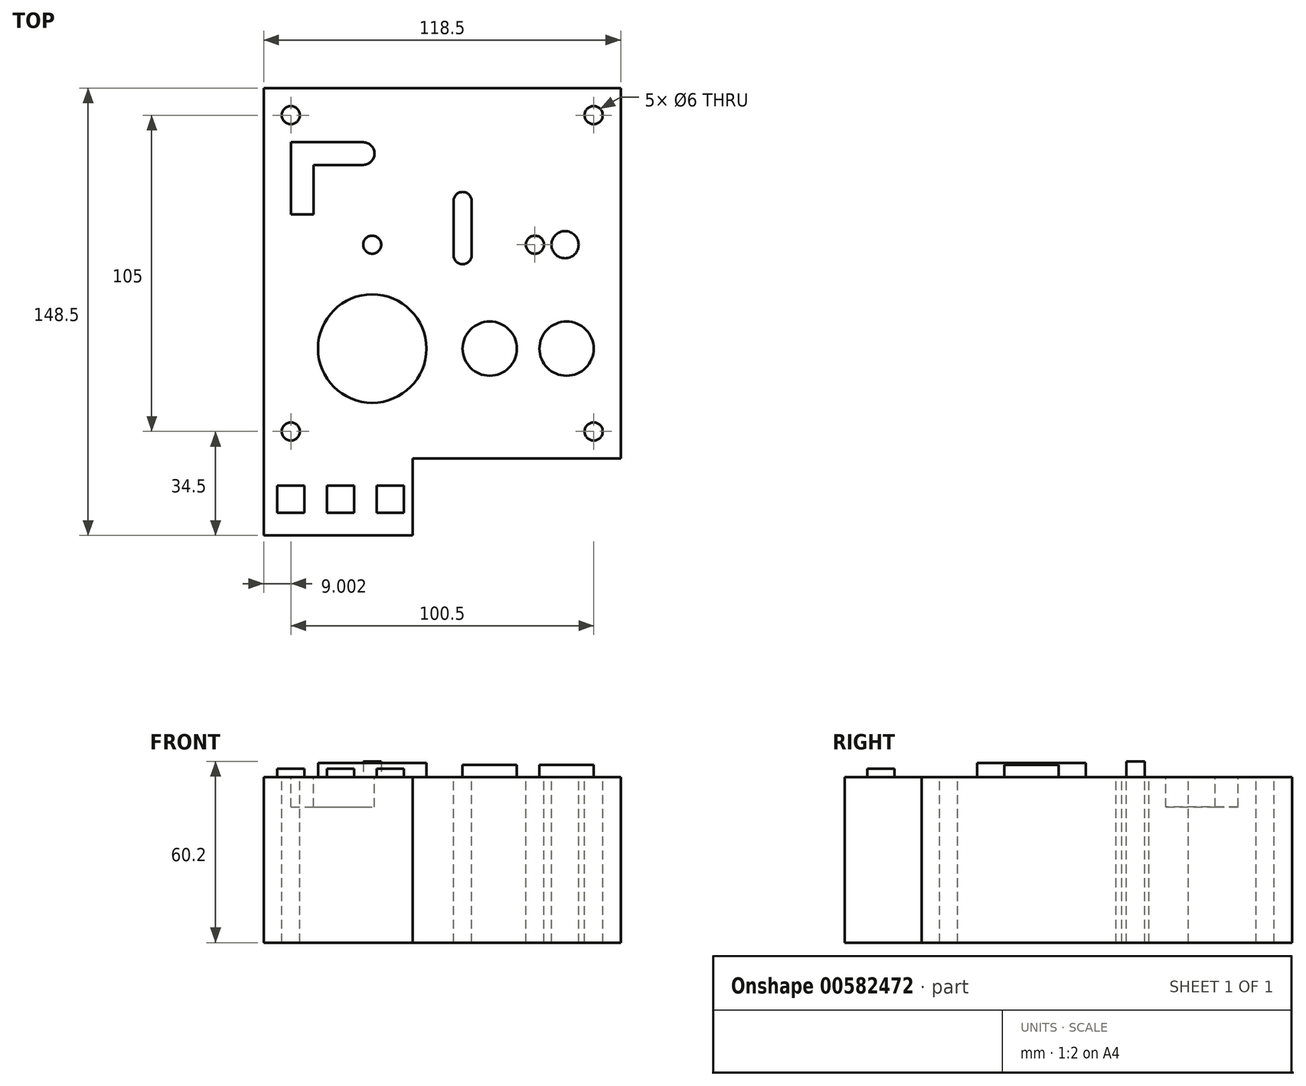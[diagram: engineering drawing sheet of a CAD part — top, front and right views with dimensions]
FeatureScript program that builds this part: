
annotation { "Feature Type Name" : "Feature", "Feature Type Description" : "" }
export const myFeature = defineFeature(function(context is Context, id is Id, definition is map)
    precondition{}
    {
        {
            var Q0;
            Q0=qCreatedBy(makeId("Top.planeOp"),FACE);
            var sketch = newSketch(context, id + "F0", { "sketchPlane" : qUnion([Q0])});
            skLineSegment(sketch, "E0", {"start": v(-56.89, 15.26) * mm, "end": v(61.61, 15.26) * mm});
            skLineSegment(sketch, "E1", {"start": v(61.61, 15.26) * mm, "end": v(61.61, -107.74) * mm});
            skLineSegment(sketch, "E2", {"start": v(-56.89, 15.26) * mm, "end": v(-56.89, -133.24) * mm});
            skLineSegment(sketch, "E3", {"start": v(-56.89, -133.24) * mm, "end": v(-7.39, -133.24) * mm});
            skLineSegment(sketch, "E4", {"start": v(61.61, -107.74) * mm, "end": v(-7.39, -107.74) * mm});
            skLineSegment(sketch, "E5", {"start": v(-7.39, -107.74) * mm, "end": v(-7.39, -133.24) * mm});
            skSolve(sketch);
        }
        {
            var Q0;
            Q0=makeQuery(id+"F0.imprint","IMPRINT",FACE,{"disambiguationData":[TD([[makeQuery(id+"F0.imprint","IMPRINT",EDGE,{"derivedFrom":sQuery(id+"F0.wireOp",EDGE,"E0")}),-1.0]])]});
            extrude(context, id + "F1", {"entities" : qUnion([Q0]), "depth" : 55 * mm, "offsetDistance" : 25 * mm});
        }
        {
            var Q0;
            Q0=makeQuery(id+"F1.opExtrude","CAP_FACE",FACE,{"disambiguationData":[OSD([sQuery(id+"F0.wireOp",EDGE,"E0"),sQuery(id+"F0.wireOp",EDGE,"E1"),sQuery(id+"F0.wireOp",EDGE,"E2"),sQuery(id+"F0.wireOp",EDGE,"E3"),sQuery(id+"F0.wireOp",EDGE,"E4"),sQuery(id+"F0.wireOp",EDGE,"E5")])],"isStart":false});
            var sketch = newSketch(context, id + "F2", { "sketchPlane" : qUnion([Q0])});
            skCircle(sketch, "E6", {"center": v(52.61, 6.26) * mm, "radius": 3 * mm});
            skLineSegment(sketch, "E7", {"start": v(52.61, 6.26) * mm, "end": v(49.61, 6.26) * mm});
            skCircle(sketch, "E8", {"center": v(-47.89, -98.74) * mm, "radius": 3 * mm});
            skCircle(sketch, "E9", {"center": v(-47.89, 6.26) * mm, "radius": 3 * mm});
            skCircle(sketch, "E10", {"center": v(52.61, -98.74) * mm, "radius": 3 * mm});
            skPoint(sketch, "E11.end.orphan", {"position": v(52.61, 15.26) * mm});
            skSolve(sketch);
        }
        {
            var Q0;
            Q0=makeQuery(id+"F2.imprint","IMPRINT",FACE,{"disambiguationData":[TD([[makeQuery(id+"F2.imprint","IMPRINT",EDGE,{"derivedFrom":sQuery(id+"F2.wireOp",EDGE,"E8")}),1.0]])]});
            var Q1;
            Q1=makeQuery(id+"F2.imprint","IMPRINT",FACE,{"disambiguationData":[TD([[makeQuery(id+"F2.imprint","IMPRINT",EDGE,{"derivedFrom":sQuery(id+"F2.wireOp",EDGE,"E10")}),1.0]])]});
            var Q2;
            Q2=makeQuery(id+"F2.imprint","IMPRINT",FACE,{"disambiguationData":[TD([[makeQuery(id+"F2.imprint","IMPRINT",EDGE,{"derivedFrom":sQuery(id+"F2.wireOp",EDGE,"E6")}),1.0]])]});
            var Q3;
            Q3=makeQuery(id+"F2.imprint","IMPRINT",FACE,{"disambiguationData":[TD([[makeQuery(id+"F2.imprint","IMPRINT",EDGE,{"derivedFrom":sQuery(id+"F2.wireOp",EDGE,"E9")}),1.0]])]});
            extrude(context, id + "F3", {"entities" : qUnion([Q0, Q1, Q2, Q3]), "operationType" : NewBodyOperationType.REMOVE, "endBound" : BoundingType.THROUGH_ALL, "oppositeDirection" : true, "depth" : 55 * mm, "offsetDistance" : 25 * mm});
        }
        {
            var Q0;
            Q0=makeQuery(id+"F1.opExtrude","CAP_FACE",FACE,{"disambiguationData":[OSD([sQuery(id+"F0.wireOp",EDGE,"E0"),sQuery(id+"F0.wireOp",EDGE,"E1"),sQuery(id+"F0.wireOp",EDGE,"E2"),sQuery(id+"F0.wireOp",EDGE,"E3"),sQuery(id+"F0.wireOp",EDGE,"E4"),sQuery(id+"F0.wireOp",EDGE,"E5")])],"isStart":false});
            var sketch = newSketch(context, id + "F4", { "sketchPlane" : qUnion([Q0])});
            skLineSegment(sketch, "E12", {"start": v(61.61, 15.26) * mm, "end": v(61.61, -71.24) * mm});
            skCircle(sketch, "E13", {"center": v(-20.89, -71.24) * mm, "radius": 18 * mm});
            skPoint(sketch, "E14.orphan", {"position": v(-56.89, -71.24) * mm});
            skSolve(sketch);
        }
        {
            var Q0;
            Q0 = qSketchRegion(id + "F4", true);
            extrude(context, id + "F5", {"entities" : qUnion([Q0]), "operationType" : NewBodyOperationType.ADD, "depth" : 4.7 * mm, "offsetDistance" : 25 * mm});
        }
        {
            var Q0;
            Q0=makeQuery(id+"F1.opExtrude","CAP_FACE",FACE,{"disambiguationData":[OSD([sQuery(id+"F0.wireOp",EDGE,"E0"),sQuery(id+"F0.wireOp",EDGE,"E1"),sQuery(id+"F0.wireOp",EDGE,"E2"),sQuery(id+"F0.wireOp",EDGE,"E3"),sQuery(id+"F0.wireOp",EDGE,"E4"),sQuery(id+"F0.wireOp",EDGE,"E5")])],"isStart":false});
            var sketch = newSketch(context, id + "F6", { "sketchPlane" : qUnion([Q0])});
            skCircle(sketch, "E15", {"center": v(18.11, -71.24) * mm, "radius": 9 * mm});
            skCircle(sketch, "E16", {"center": v(43.61, -71.24) * mm, "radius": 9 * mm});
            skPoint(sketch, "E17.orphan", {"position": v(-20.89, -71.24) * mm});
            skSolve(sketch);
        }
        {
            var Q0;
            Q0=makeQuery(id+"F6.imprint","IMPRINT",FACE,{"disambiguationData":[TD([[makeQuery(id+"F6.imprint","IMPRINT",EDGE,{"derivedFrom":sQuery(id+"F6.wireOp",EDGE,"E15")}),1.0]])]});
            var Q1;
            Q1=makeQuery(id+"F6.imprint","IMPRINT",FACE,{"disambiguationData":[TD([[makeQuery(id+"F6.imprint","IMPRINT",EDGE,{"derivedFrom":sQuery(id+"F6.wireOp",EDGE,"E16")}),1.0]])]});
            extrude(context, id + "F7", {"entities" : qUnion([Q0, Q1]), "operationType" : NewBodyOperationType.ADD, "depth" : 4 * mm, "offsetDistance" : 25 * mm});
        }
        {
            var Q0;
            Q0=makeQuery(id+"F1.opExtrude","CAP_FACE",FACE,{"disambiguationData":[OSD([sQuery(id+"F0.wireOp",EDGE,"E0"),sQuery(id+"F0.wireOp",EDGE,"E1"),sQuery(id+"F0.wireOp",EDGE,"E2"),sQuery(id+"F0.wireOp",EDGE,"E3"),sQuery(id+"F0.wireOp",EDGE,"E4"),sQuery(id+"F0.wireOp",EDGE,"E5")])],"isStart":false});
            var sketch = newSketch(context, id + "F8", { "sketchPlane" : qUnion([Q0])});
            skLineSegment(sketch, "E18", {"start": v(-56.89, 15.26) * mm, "end": v(9.11, 15.26) * mm});
            skArc(sketch, "E19", {"start": v(12.11, -22.24) * mm, "mid": v(9.11, -19.24) * mm, "end": v(6.11, -22.24) * mm});
            skArc(sketch, "E20", {"start": v(6.11, -40.24) * mm, "mid": v(9.11, -43.24) * mm, "end": v(12.11, -40.24) * mm});
            skLineSegment(sketch, "E21", {"start": v(6.11, -22.24) * mm, "end": v(6.11, -40.24) * mm});
            skLineSegment(sketch, "E22", {"start": v(12.11, -22.24) * mm, "end": v(12.11, -40.24) * mm});
            skSolve(sketch);
        }
        {
            var Q0;
            Q0=makeQuery(id+"F8.imprint","IMPRINT",FACE,{"disambiguationData":[TD([[makeQuery(id+"F8.imprint","IMPRINT",EDGE,{"derivedFrom":sQuery(id+"F8.wireOp",EDGE,"E19")}),1.0]])]});
            extrude(context, id + "F9", {"entities" : qUnion([Q0]), "operationType" : NewBodyOperationType.REMOVE, "endBound" : BoundingType.THROUGH_ALL, "oppositeDirection" : true, "depth" : 25 * mm, "offsetDistance" : 25 * mm});
        }
        {
            var Q0;
            Q0=makeQuery(id+"F1.opExtrude","CAP_FACE",FACE,{"disambiguationData":[OSD([sQuery(id+"F0.wireOp",EDGE,"E0"),sQuery(id+"F0.wireOp",EDGE,"E1"),sQuery(id+"F0.wireOp",EDGE,"E2"),sQuery(id+"F0.wireOp",EDGE,"E3"),sQuery(id+"F0.wireOp",EDGE,"E4"),sQuery(id+"F0.wireOp",EDGE,"E5")])],"isStart":false});
            var sketch = newSketch(context, id + "F10", { "sketchPlane" : qUnion([Q0])});
            skLineSegment(sketch, "E23", {"start": v(-56.89, 15.26) * mm, "end": v(33.11, 15.26) * mm});
            skCircle(sketch, "E24", {"center": v(33.11, -36.74) * mm, "radius": 3 * mm});
            skCircle(sketch, "E25", {"center": v(43.11, -36.74) * mm, "radius": 4.5 * mm});
            skSolve(sketch);
        }
        {
            var Q0;
            Q0 = qSketchRegion(id + "F10", true);
            extrude(context, id + "F11", {"entities" : qUnion([Q0]), "operationType" : NewBodyOperationType.REMOVE, "endBound" : BoundingType.THROUGH_ALL, "oppositeDirection" : true, "depth" : 25 * mm, "offsetDistance" : 25 * mm});
        }
        {
            var Q0;
            Q0=makeQuery(id+"F1.opExtrude","CAP_FACE",FACE,{"disambiguationData":[OSD([sQuery(id+"F0.wireOp",EDGE,"E0"),sQuery(id+"F0.wireOp",EDGE,"E1"),sQuery(id+"F0.wireOp",EDGE,"E2"),sQuery(id+"F0.wireOp",EDGE,"E3"),sQuery(id+"F0.wireOp",EDGE,"E4"),sQuery(id+"F0.wireOp",EDGE,"E5")])],"isStart":false});
            var sketch = newSketch(context, id + "F12", { "sketchPlane" : qUnion([Q0])});
            skLineSegment(sketch, "E26", {"start": v(-47.89, -2.74) * mm, "end": v(-23.89, -2.74) * mm});
            skArc(sketch, "E27", {"start": v(-23.89, -10.24) * mm, "mid": v(-20.14, -6.5) * mm, "end": v(-23.89, -2.74) * mm});
            skLineSegment(sketch, "E28", {"start": v(-47.89, -2.74) * mm, "end": v(-47.89, -26.74) * mm});
            skLineSegment(sketch, "E29", {"start": v(-47.89, -26.74) * mm, "end": v(-40.39, -26.74) * mm});
            skLineSegment(sketch, "E30", {"start": v(-40.39, -26.74) * mm, "end": v(-40.39, -10.24) * mm});
            skLineSegment(sketch, "E31", {"start": v(-40.39, -10.24) * mm, "end": v(-23.89, -10.24) * mm});
            skSolve(sketch);
        }
        {
            var Q0;
            Q0=makeQuery(id+"F12.imprint","IMPRINT",FACE,{"disambiguationData":[TD([[makeQuery(id+"F12.imprint","IMPRINT",EDGE,{"derivedFrom":sQuery(id+"F12.wireOp",EDGE,"E26")}),-1.0]])]});
            extrude(context, id + "F13", {"entities" : qUnion([Q0]), "operationType" : NewBodyOperationType.REMOVE, "oppositeDirection" : true, "depth" : 10 * mm, "offsetDistance" : 25 * mm});
        }
        {
            var Q0;
            Q0=makeQuery(id+"F1.opExtrude","CAP_FACE",FACE,{"disambiguationData":[OSD([sQuery(id+"F0.wireOp",EDGE,"E0"),sQuery(id+"F0.wireOp",EDGE,"E1"),sQuery(id+"F0.wireOp",EDGE,"E2"),sQuery(id+"F0.wireOp",EDGE,"E3"),sQuery(id+"F0.wireOp",EDGE,"E4"),sQuery(id+"F0.wireOp",EDGE,"E5")])],"isStart":false});
            var sketch = newSketch(context, id + "F14", { "sketchPlane" : qUnion([Q0])});
            skLineSegment(sketch, "E32", {"start": v(-20.89, -33.74) * mm, "end": v(-20.89, -36.74) * mm});
            skCircle(sketch, "E33", {"center": v(-20.89, -36.74) * mm, "radius": 3 * mm});
            skSolve(sketch);
        }
        {
            var Q0;
            Q0=makeQuery(id+"F14.imprint","IMPRINT",FACE,{"disambiguationData":[TD([[makeQuery(id+"F14.imprint","IMPRINT",EDGE,{"derivedFrom":sQuery(id+"F14.wireOp",EDGE,"E33")}),1.0]])]});
            extrude(context, id + "F15", {"entities" : qUnion([Q0]), "operationType" : NewBodyOperationType.ADD, "depth" : 5.2 * mm, "offsetDistance" : 25 * mm});
        }
        {
            var Q0;
            Q0=makeQuery(id+"F1.opExtrude","CAP_FACE",FACE,{"disambiguationData":[OSD([sQuery(id+"F0.wireOp",EDGE,"E0"),sQuery(id+"F0.wireOp",EDGE,"E1"),sQuery(id+"F0.wireOp",EDGE,"E2"),sQuery(id+"F0.wireOp",EDGE,"E3"),sQuery(id+"F0.wireOp",EDGE,"E4"),sQuery(id+"F0.wireOp",EDGE,"E5")])],"isStart":false});
            var sketch = newSketch(context, id + "F16", { "sketchPlane" : qUnion([Q0])});
            skLineSegment(sketch, "E34", {"start": v(-52.39, -116.74) * mm, "end": v(-52.39, -125.74) * mm});
            skLineSegment(sketch, "E35", {"start": v(-52.39, -125.74) * mm, "end": v(-43.39, -125.74) * mm});
            skLineSegment(sketch, "E36", {"start": v(-43.39, -125.74) * mm, "end": v(-43.39, -116.74) * mm});
            skLineSegment(sketch, "E37", {"start": v(-52.39, -116.74) * mm, "end": v(-43.39, -116.74) * mm});
            skPoint(sketch, "E38.start.orphan", {"position": v(-47.89, -98.74) * mm});
            skLineSegment(sketch, "E39", {"start": v(-35.89, -116.74) * mm, "end": v(-35.89, -125.74) * mm});
            skLineSegment(sketch, "E40", {"start": v(-35.89, -125.74) * mm, "end": v(-26.89, -125.74) * mm});
            skLineSegment(sketch, "E41", {"start": v(-26.89, -125.74) * mm, "end": v(-26.89, -116.74) * mm});
            skLineSegment(sketch, "E42", {"start": v(-26.89, -116.74) * mm, "end": v(-35.89, -116.74) * mm});
            skLineSegment(sketch, "E43", {"start": v(-19.39, -116.74) * mm, "end": v(-19.39, -125.74) * mm});
            skLineSegment(sketch, "E44", {"start": v(-19.39, -125.74) * mm, "end": v(-10.39, -125.74) * mm});
            skLineSegment(sketch, "E45", {"start": v(-10.39, -125.74) * mm, "end": v(-10.39, -116.74) * mm});
            skLineSegment(sketch, "E46", {"start": v(-10.39, -116.74) * mm, "end": v(-19.39, -116.74) * mm});
            skPoint(sketch, "E47.start.orphan", {"position": v(-56.89, -116.74) * mm});
            skSolve(sketch);
        }
        {
            var Q0;
            Q0 = qSketchRegion(id + "F16", true);
            extrude(context, id + "F17", {"entities" : qUnion([Q0]), "operationType" : NewBodyOperationType.ADD, "depth" : 2.7 * mm, "offsetDistance" : 25 * mm});
        }
    });
